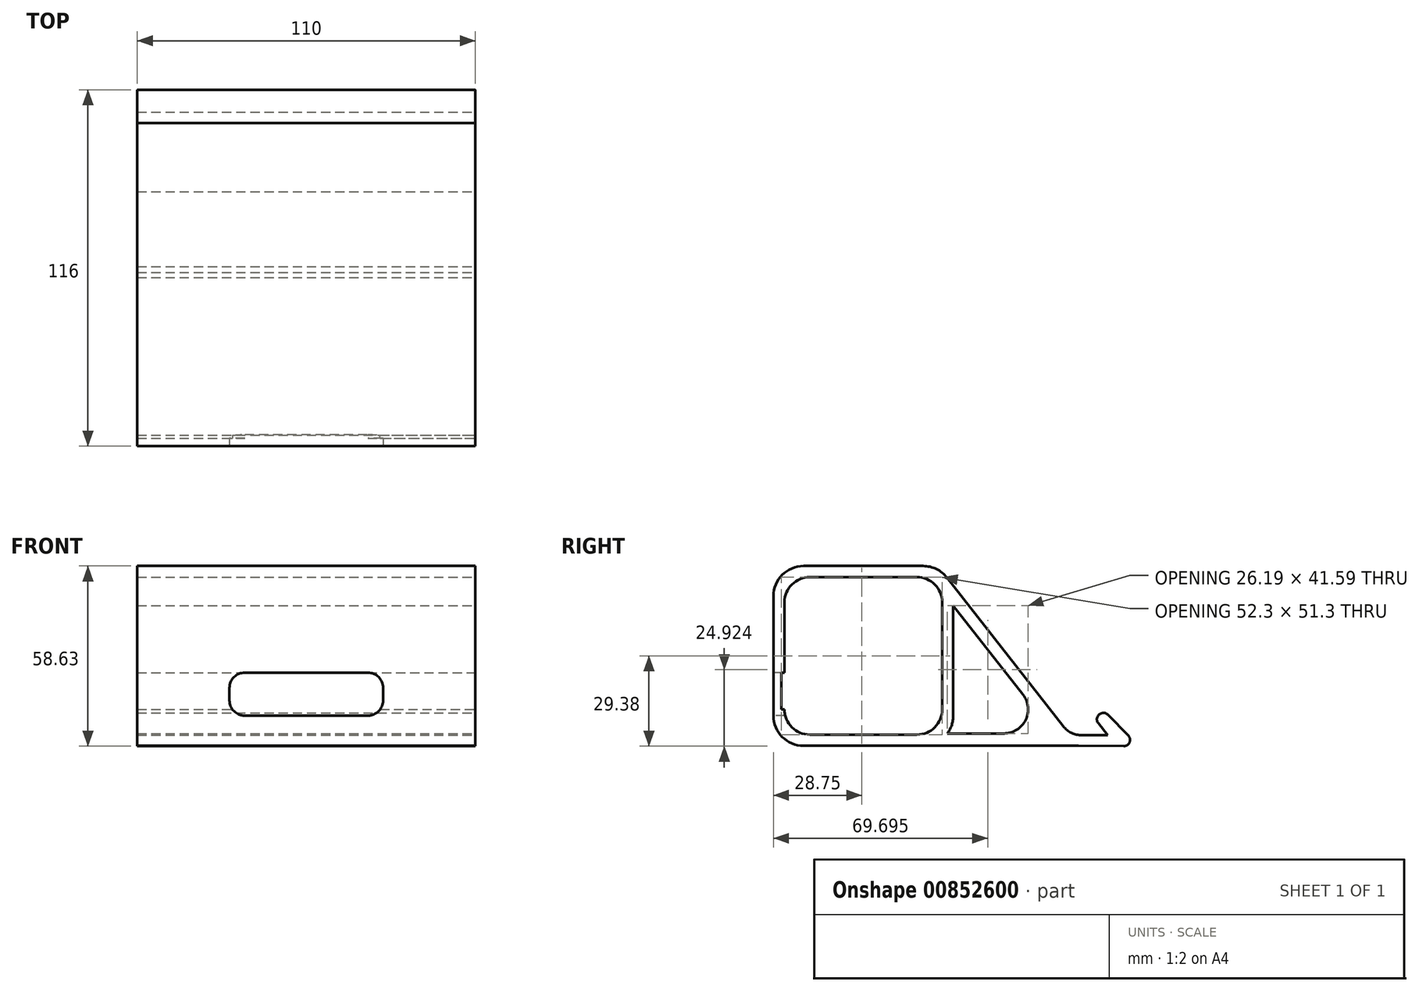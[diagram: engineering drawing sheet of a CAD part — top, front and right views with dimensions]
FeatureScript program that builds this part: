
annotation { "Feature Type Name" : "Feature", "Feature Type Description" : "" }
export const myFeature = defineFeature(function(context is Context, id is Id, definition is map)
    precondition{}
    {
        {
            var Q0;
            Q0=qCreatedBy(makeId("Right.planeOp"),FACE);
            var sketch = newSketch(context, id + "F0", { "sketchPlane" : qUnion([Q0])});
            skLineSegment(sketch, "E0.bottom", {"start": v(17.45, 25.25) * mm, "end": v(-17.45, 25.25) * mm});
            skLineSegment(sketch, "E0.top", {"start": v(17.45, -25.25) * mm, "end": v(-17.45, -25.25) * mm});
            skLineSegment(sketch, "E0.left", {"start": v(25.25, 17.45) * mm, "end": v(25.25, -17.45) * mm});
            skLineSegment(sketch, "E0.right", {"start": v(-25.25, 17.45) * mm, "end": v(-25.25, -17.45) * mm});
            skPoint(sketch, "E0.middle", {"position": v(0, 0) * mm});
            skPoint(sketch, "E1.visualSharp", {"position": v(-25.25, 25.25) * mm});
            skArc(sketch, "E1.filletArc", {"start": v(-17.45, 25.25) * mm, "mid": v(-22.97, 22.97) * mm, "end": v(-25.25, 17.45) * mm});
            skPoint(sketch, "E2.visualSharp", {"position": v(25.25, 25.25) * mm});
            skArc(sketch, "E2.filletArc", {"start": v(25.25, 17.45) * mm, "mid": v(22.97, 22.97) * mm, "end": v(17.45, 25.25) * mm});
            skPoint(sketch, "E3.visualSharp", {"position": v(25.25, -25.25) * mm});
            skArc(sketch, "E3.filletArc", {"start": v(17.45, -25.25) * mm, "mid": v(22.97, -22.97) * mm, "end": v(25.25, -17.45) * mm});
            skPoint(sketch, "E4.visualSharp", {"position": v(-25.25, -25.25) * mm});
            skArc(sketch, "E4.filletArc", {"start": v(-25.25, -17.45) * mm, "mid": v(-22.97, -22.97) * mm, "end": v(-17.45, -25.25) * mm});
            skPoint(sketch, "E5.visualSharp", {"position": v(-27.25, 27.25) * mm});
            skPoint(sketch, "E6.visualSharp", {"position": v(27.25, 27.25) * mm});
            skPoint(sketch, "E7.visualSharp", {"position": v(27.25, -27.25) * mm});
            skPoint(sketch, "E8.visualSharp", {"position": v(-27.25, -27.25) * mm});
            skArc(sketch, "E9.0", {"start": v(29.25, 19.45) * mm, "mid": v(26.38, 26.38) * mm, "end": v(19.45, 29.25) * mm});
            skLineSegment(sketch, "E9.1", {"start": v(29.25, 19.45) * mm, "end": v(29.25, -19.45) * mm});
            skLineSegment(sketch, "E9.2", {"start": v(19.45, 29.25) * mm, "end": v(-19.45, 29.25) * mm});
            skArc(sketch, "E9.3", {"start": v(19.45, -29.25) * mm, "mid": v(26.38, -26.38) * mm, "end": v(29.25, -19.45) * mm});
            skArc(sketch, "E9.4", {"start": v(-19.45, 29.25) * mm, "mid": v(-26.38, 26.38) * mm, "end": v(-29.25, 19.45) * mm});
            skLineSegment(sketch, "E9.5", {"start": v(-29.25, 19.45) * mm, "end": v(-29.25, -19.45) * mm});
            skArc(sketch, "E9.6", {"start": v(-29.25, -19.45) * mm, "mid": v(-26.38, -26.38) * mm, "end": v(-19.45, -29.25) * mm});
            skLineSegment(sketch, "E9.7", {"start": v(19.45, -29.25) * mm, "end": v(-19.45, -29.25) * mm});
            skArc(sketch, "E10.0", {"start": v(25.65, 17.45) * mm, "mid": v(23.25, 23.25) * mm, "end": v(17.45, 25.65) * mm});
            skLineSegment(sketch, "E10.1", {"start": v(25.65, 17.45) * mm, "end": v(25.65, -17.45) * mm});
            skLineSegment(sketch, "E10.2", {"start": v(17.45, 25.65) * mm, "end": v(-17.45, 25.65) * mm});
            skArc(sketch, "E10.3", {"start": v(17.45, -25.65) * mm, "mid": v(23.25, -23.25) * mm, "end": v(25.65, -17.45) * mm});
            skArc(sketch, "E10.4", {"start": v(-17.45, 25.65) * mm, "mid": v(-23.25, 23.25) * mm, "end": v(-25.65, 17.45) * mm});
            skLineSegment(sketch, "E10.5", {"start": v(-25.65, 17.45) * mm, "end": v(-25.65, -17.45) * mm});
            skArc(sketch, "E10.6", {"start": v(-25.65, -17.45) * mm, "mid": v(-23.25, -23.25) * mm, "end": v(-17.45, -25.65) * mm});
            skLineSegment(sketch, "E10.7", {"start": v(17.45, -25.65) * mm, "end": v(-17.45, -25.65) * mm});
            skSolve(sketch);
        }
        {
            var Q0;
            Q0=makeQuery(id+"F0.imprint","IMPRINT",FACE,{"disambiguationData":[TD([[makeQuery(id+"F0.imprint","IMPRINT",EDGE,{"derivedFrom":sQuery(id+"F0.wireOp",EDGE,"E9.0")}),1.0]])]});
            extrude(context, id + "F1", {"entities" : qUnion([Q0]), "endBound" : BoundingType.SYMMETRIC, "oppositeDirection" : true, "depth" : 110 * mm, "offsetDistance" : 25 * mm});
        }
        {
            var Q0;
            Q0=makeQuery(id+"F1.opExtrude","SWEPT_FACE",FACE,{"disambiguationData":[OSD([sQuery(id+"F0.wireOp",EDGE,"E9.5")])]});
            var sketch = newSketch(context, id + "F2", { "sketchPlane" : qUnion([Q0])});
            skLineSegment(sketch, "E11", {"start": v(-55, -6.86) * mm, "end": v(-25, -6.86) * mm, "construction": true});
            skLineSegment(sketch, "E12", {"start": v(55, -7.4) * mm, "end": v(25, -7.4) * mm, "construction": true});
            skLineSegment(sketch, "E13", {"start": v(0, -19.45) * mm, "end": v(0, -5.45) * mm, "construction": true});
            skLineSegment(sketch, "E14.bottom", {"start": v(-25, -19.45) * mm, "end": v(25, -19.45) * mm});
            skLineSegment(sketch, "E14.top", {"start": v(-25, -5.45) * mm, "end": v(25, -5.45) * mm});
            skLineSegment(sketch, "E14.left", {"start": v(-25, -19.45) * mm, "end": v(-25, -5.45) * mm});
            skLineSegment(sketch, "E14.right", {"start": v(25, -19.45) * mm, "end": v(25, -5.45) * mm});
            skSolve(sketch);
        }
        {
            var Q0;
            Q0=makeQuery(id+"F2.imprint","IMPRINT",FACE,{"disambiguationData":[TD([[makeQuery(id+"F2.imprint","IMPRINT",EDGE,{"derivedFrom":sQuery(id+"F2.wireOp",EDGE,"E14.bottom")}),1.0]])]});
            extrude(context, id + "F3", {"entities" : qUnion([Q0]), "operationType" : NewBodyOperationType.REMOVE, "oppositeDirection" : true, "depth" : 5 * mm, "offsetDistance" : 25 * mm});
        }
        {
            var Q0;
            Q0=makeQuery(id+"F1.opExtrude","CAP_FACE",FACE,{"disambiguationData":[OSD([sQuery(id+"F0.wireOp",EDGE,"E0.bottom"),sQuery(id+"F0.wireOp",EDGE,"E0.top"),sQuery(id+"F0.wireOp",EDGE,"E0.left"),sQuery(id+"F0.wireOp",EDGE,"E0.right"),sQuery(id+"F0.wireOp",EDGE,"E1.filletArc"),sQuery(id+"F0.wireOp",EDGE,"E2.filletArc"),sQuery(id+"F0.wireOp",EDGE,"E3.filletArc"),sQuery(id+"F0.wireOp",EDGE,"E4.filletArc"),sQuery(id+"F0.wireOp",EDGE,"E9.0"),sQuery(id+"F0.wireOp",EDGE,"E9.1"),sQuery(id+"F0.wireOp",EDGE,"E9.2"),sQuery(id+"F0.wireOp",EDGE,"E9.3"),sQuery(id+"F0.wireOp",EDGE,"E9.4"),sQuery(id+"F0.wireOp",EDGE,"E9.5"),sQuery(id+"F0.wireOp",EDGE,"E9.6"),sQuery(id+"F0.wireOp",EDGE,"E9.7")])],"isStart":true});
            var sketch = newSketch(context, id + "F4", { "sketchPlane" : qUnion([Q0])});
            skLineSegment(sketch, "E15", {"start": v(-29.25, -19.45) * mm, "end": v(-24.99, -19.45) * mm, "construction": true});
            skLineSegment(sketch, "E16", {"start": v(-27.12, -19.45) * mm, "end": v(-27.12, -5.45) * mm, "construction": true});
            skLineSegment(sketch, "E17.bottom", {"start": v(-25.65, -5.45) * mm, "end": v(-26.65, -5.45) * mm});
            skLineSegment(sketch, "E17.top", {"start": v(-25.65, -17.45) * mm, "end": v(-26.65, -17.45) * mm});
            skLineSegment(sketch, "E17.left", {"start": v(-25.65, -5.45) * mm, "end": v(-25.65, -17.45) * mm});
            skLineSegment(sketch, "E17.right", {"start": v(-26.65, -5.45) * mm, "end": v(-26.65, -17.45) * mm});
            skSolve(sketch);
        }
        {
            var Q0;
            Q0=makeQuery(id+"F4.imprint","IMPRINT",FACE,{"disambiguationData":[TD([[makeQuery(id+"F4.imprint","IMPRINT",EDGE,{"derivedFrom":sQuery(id+"F4.wireOp",EDGE,"E17.bottom")}),1.0]])]});
            extrude(context, id + "F5", {"entities" : qUnion([Q0]), "operationType" : NewBodyOperationType.REMOVE, "oppositeDirection" : true, "depth" : 112 * mm, "offsetDistance" : 25 * mm});
        }
        {
            var Q0;
            Q0=makeQuery(id+"F1.opExtrude","CAP_FACE",FACE,{"disambiguationData":[OSD([sQuery(id+"F0.wireOp",EDGE,"E0.bottom"),sQuery(id+"F0.wireOp",EDGE,"E0.top"),sQuery(id+"F0.wireOp",EDGE,"E0.left"),sQuery(id+"F0.wireOp",EDGE,"E0.right"),sQuery(id+"F0.wireOp",EDGE,"E1.filletArc"),sQuery(id+"F0.wireOp",EDGE,"E2.filletArc"),sQuery(id+"F0.wireOp",EDGE,"E3.filletArc"),sQuery(id+"F0.wireOp",EDGE,"E4.filletArc"),sQuery(id+"F0.wireOp",EDGE,"E9.0"),sQuery(id+"F0.wireOp",EDGE,"E9.1"),sQuery(id+"F0.wireOp",EDGE,"E9.2"),sQuery(id+"F0.wireOp",EDGE,"E9.3"),sQuery(id+"F0.wireOp",EDGE,"E9.4"),sQuery(id+"F0.wireOp",EDGE,"E9.5"),sQuery(id+"F0.wireOp",EDGE,"E9.6"),sQuery(id+"F0.wireOp",EDGE,"E9.7")])],"isStart":true});
            var sketch = newSketch(context, id + "F6", { "sketchPlane" : qUnion([Q0])});
            skLineSegment(sketch, "E18", {"start": v(0, -29.25) * mm, "end": v(70, -29.25) * mm});
            skLineSegment(sketch, "E19", {"start": v(65, -22.87) * mm, "end": v(27.17, 25.49) * mm});
            skLineSegment(sketch, "E20.0", {"start": v(51.93, -12.64) * mm, "end": v(24.02, 23.02) * mm});
            skLineSegment(sketch, "E20.1", {"start": v(0, -25.25) * mm, "end": v(45.78, -25.25) * mm});
            skPoint(sketch, "E21.visualSharp", {"position": v(61.8, -25.25) * mm});
            skArc(sketch, "E21.filletArc", {"start": v(45.78, -25.25) * mm, "mid": v(52.8, -20.87) * mm, "end": v(51.93, -12.64) * mm});
            skLineSegment(sketch, "E22", {"start": v(79.49, -25.86) * mm, "end": v(71.15, -25.86) * mm});
            skLineSegment(sketch, "E23", {"start": v(79.49, -25.86) * mm, "end": v(76.4, -21.92) * mm});
            skLineSegment(sketch, "E24", {"start": v(76.75, -19.11) * mm, "end": v(76.9, -18.99) * mm});
            skLineSegment(sketch, "E25", {"start": v(79.58, -19.17) * mm, "end": v(86.19, -25.99) * mm});
            skLineSegment(sketch, "E26", {"start": v(70, -29.25) * mm, "end": v(84.74, -29.38) * mm});
            skPoint(sketch, "E27.visualSharp", {"position": v(89.52, -29.42) * mm});
            skArc(sketch, "E27.filletArc", {"start": v(84.74, -29.38) * mm, "mid": v(86.6, -28.17) * mm, "end": v(86.19, -25.99) * mm});
            skPoint(sketch, "E28.visualSharp", {"position": v(78.33, -17.88) * mm});
            skArc(sketch, "E28.filletArc", {"start": v(79.58, -19.17) * mm, "mid": v(78.28, -18.57) * mm, "end": v(76.9, -18.99) * mm});
            skPoint(sketch, "E29.visualSharp", {"position": v(75.18, -20.35) * mm});
            skArc(sketch, "E29.filletArc", {"start": v(76.75, -19.11) * mm, "mid": v(76, -20.45) * mm, "end": v(76.4, -21.92) * mm});
            skPoint(sketch, "E30.visualSharp", {"position": v(67.35, -25.86) * mm});
            skArc(sketch, "E30.filletArc", {"start": v(65, -22.87) * mm, "mid": v(67.73, -25.07) * mm, "end": v(71.15, -25.86) * mm});
            skSolve(sketch);
        }
        {
            var Q0;
            {var subQ6=sQuery(id+"F6.wireOp",EDGE,"E19");Q0=makeQuery(id+"F6.imprint","IMPRINT",FACE,{"disambiguationData":[TD([[makeQuery(id+"F6.imprint","IMPRINT",EDGE,{"derivedFrom":subQ6}),1.0]])]});}
            extrude(context, id + "F7", {"entities" : qUnion([Q0]), "operationType" : NewBodyOperationType.ADD, "oppositeDirection" : true, "depth" : 110 * mm, "offsetDistance" : 25 * mm});
        }
        {
            var Q0;
            Q0=makeQuery(id+"F3.boolean.opBoolean","COPY",EDGE,{"derivedFrom":makeQuery(id+"F3.opExtrude","SWEPT_EDGE",EDGE,{"disambiguationData":[OSD([sQuery(id+"F2.wireOp",EDGE,"E14.top"),sQuery(id+"F2.wireOp",EDGE,"E14.left")])]})});
            var Q1;
            Q1=makeQuery(id+"F3.boolean.opBoolean","COPY",EDGE,{"derivedFrom":makeQuery(id+"F3.opExtrude","SWEPT_EDGE",EDGE,{"disambiguationData":[OSD([sQuery(id+"F0.wireOp",EDGE,"E9.5"),sQuery(id+"F0.wireOp",EDGE,"E9.6"),sQuery(id+"F2.wireOp",EDGE,"E14.bottom"),sQuery(id+"F2.wireOp",EDGE,"E14.left")])]})});
            var Q2;
            Q2=makeQuery(id+"F3.boolean.opBoolean","COPY",EDGE,{"derivedFrom":makeQuery(id+"F3.opExtrude","SWEPT_EDGE",EDGE,{"disambiguationData":[OSD([sQuery(id+"F0.wireOp",EDGE,"E9.5"),sQuery(id+"F0.wireOp",EDGE,"E9.6"),sQuery(id+"F2.wireOp",EDGE,"E14.bottom"),sQuery(id+"F2.wireOp",EDGE,"E14.right")])]})});
            var Q3;
            Q3=makeQuery(id+"F3.boolean.opBoolean","COPY",EDGE,{"derivedFrom":makeQuery(id+"F3.opExtrude","SWEPT_EDGE",EDGE,{"disambiguationData":[OSD([sQuery(id+"F2.wireOp",EDGE,"E14.top"),sQuery(id+"F2.wireOp",EDGE,"E14.right")])]})});
            fillet(context, id + "F8", {"entities" : qUnion([Q0, Q1, Q2, Q3]), "radius" : 5 * mm, "tangentPropagation" : true, "allowEdgeOverflow" : false});
        }
    });
